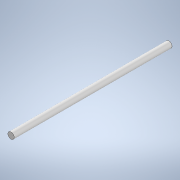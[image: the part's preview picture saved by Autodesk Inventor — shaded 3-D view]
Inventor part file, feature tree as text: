
AUTODESK INVENTOR PART (.ipt)
format: ipt  version: 2022 (Build 260153000, 153)  size: 93,184 bytes
history: native  units: mm
features: other x1, extrude x1, sketch x1
ambient origin geometry x8: Origin, YZ Plane, XZ Plane, XY Plane, X Axis, Y Axis, Z Axis, Center Point
bodies: Body1 (feature_tree)
feature tree (3):
  other  "ソリッド1"
  extrude  "押し出し1"  Depth=4.0mm
  sketch  "スケッチ1"
